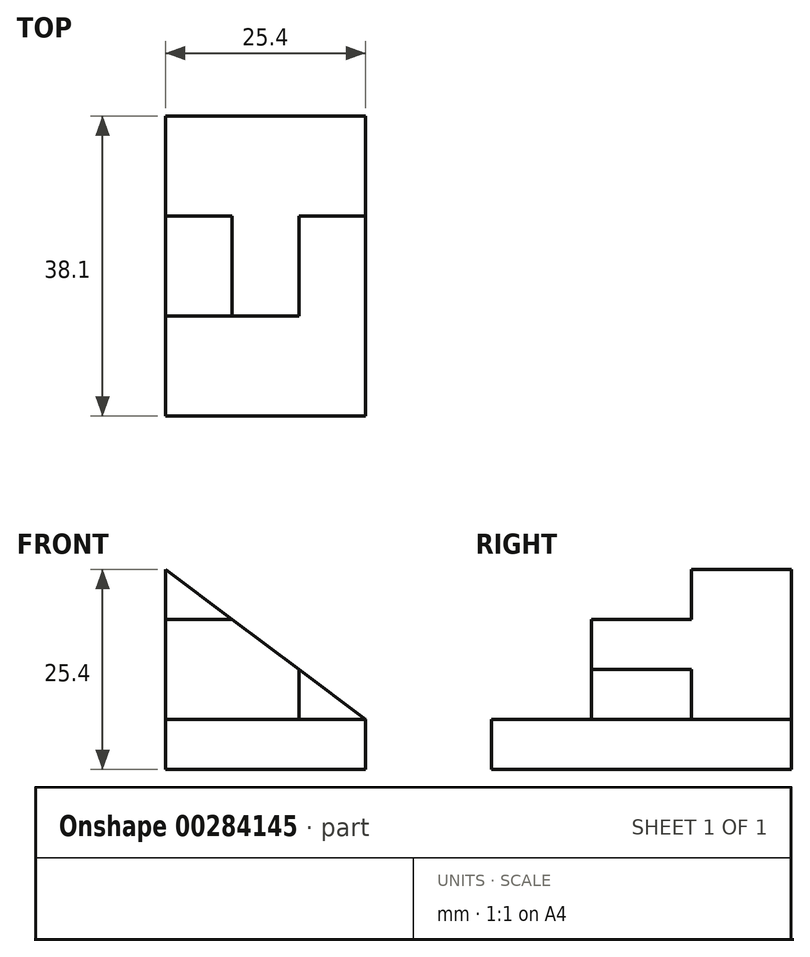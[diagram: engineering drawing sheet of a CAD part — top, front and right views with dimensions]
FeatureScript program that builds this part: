
annotation { "Feature Type Name" : "Feature", "Feature Type Description" : "" }
export const myFeature = defineFeature(function(context is Context, id is Id, definition is map)
    precondition{}
    {
        {
            var Q0;
            Q0=qCreatedBy(makeId("Front.planeOp"),FACE);
            var sketch = newSketch(context, id + "F0", { "sketchPlane" : qUnion([Q0])});
            skLineSegment(sketch, "E0", {"start": v(-12.7, 0) * mm, "end": v(12.7, 0) * mm});
            skLineSegment(sketch, "E1", {"start": v(-12.7, 0) * mm, "end": v(-12.7, 6.35) * mm});
            skLineSegment(sketch, "E2", {"start": v(-12.7, 6.35) * mm, "end": v(12.7, 6.35) * mm});
            skLineSegment(sketch, "E3", {"start": v(12.7, 6.35) * mm, "end": v(-12.7, 6.35) * mm});
            skLineSegment(sketch, "E4", {"start": v(-12.7, 19.05) * mm, "end": v(-12.7, 6.35) * mm});
            skLineSegment(sketch, "E5", {"start": v(-12.7, 19.05) * mm, "end": v(-12.7, 25.4) * mm});
            skLineSegment(sketch, "E6", {"start": v(12.7, 6.35) * mm, "end": v(-12.7, 25.4) * mm});
            skLineSegment(sketch, "E7", {"start": v(-12.7, 19.05) * mm, "end": v(-4.23, 19.05) * mm});
            skLineSegment(sketch, "E8", {"start": v(4.23, 12.7) * mm, "end": v(4.23, 6.35) * mm});
            skLineSegment(sketch, "E9", {"start": v(12.7, 0) * mm, "end": v(12.7, 6.35) * mm});
            skSolve(sketch);
        }
        {
            var Q0;
            Q0=makeQuery(id+"F0.imprint","IMPRINT",FACE,{"disambiguationData":[TD([[makeQuery(id+"F0.imprint","IMPRINT",EDGE,{"derivedFrom":sQuery(id+"F0.wireOp",EDGE,"E0")}),1.0]])]});
            extrude(context, id + "F1", {"entities" : qUnion([Q0]), "depth" : 38.1 * mm});
        }
        {
            var Q0;
            {var subQ3=sQuery(id+"F0.wireOp",EDGE,"E4");Q0=makeQuery(id+"F0.imprint","IMPRINT",FACE,{"disambiguationData":[TD([[makeQuery(id+"F0.imprint","IMPRINT",EDGE,{"derivedFrom":subQ3}),1.0]])]});}
            extrude(context, id + "F2", {"entities" : qUnion([Q0]), "operationType" : NewBodyOperationType.ADD, "depth" : 25.4 * mm});
        }
        {
            var Q0;
            {var subQ0=sQuery(id+"F0.wireOp",EDGE,"E5");Q0=makeQuery(id+"F0.imprint","IMPRINT",FACE,{"disambiguationData":[TD([[makeQuery(id+"F0.imprint","IMPRINT",EDGE,{"derivedFrom":subQ0}),-1.0]])]});}
            var Q1;
            {var subQ3=sQuery(id+"F0.wireOp",EDGE,"E8");Q1=makeQuery(id+"F0.imprint","IMPRINT",FACE,{"disambiguationData":[TD([[makeQuery(id+"F0.imprint","IMPRINT",EDGE,{"derivedFrom":subQ3}),1.0]])]});}
            extrude(context, id + "F3", {"entities" : qUnion([Q0, Q1]), "operationType" : NewBodyOperationType.ADD, "depth" : 12.7 * mm});
        }
    });
